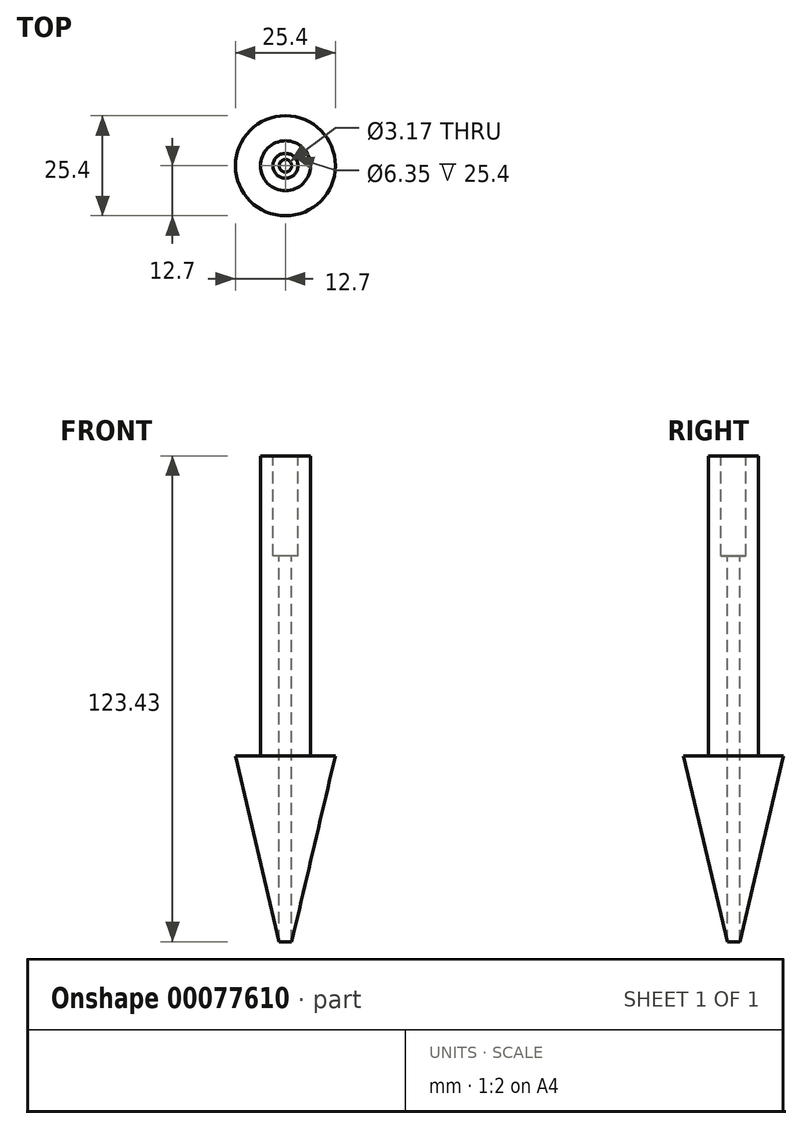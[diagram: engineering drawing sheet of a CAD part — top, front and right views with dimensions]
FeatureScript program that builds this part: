
annotation { "Feature Type Name" : "Feature", "Feature Type Description" : "" }
export const myFeature = defineFeature(function(context is Context, id is Id, definition is map)
    precondition{}
    {
        {
            var Q0;
            Q0=qCreatedBy(makeId("Front.planeOp"),FACE);
            var sketch = newSketch(context, id + "F0", { "sketchPlane" : qUnion([Q0])});
            skLineSegment(sketch, "E0", {"start": v(0, 0) * mm, "end": v(0, -53.97) * mm});
            skLineSegment(sketch, "E1", {"start": v(0, -53.98) * mm, "end": v(-12.7, 0) * mm});
            skLineSegment(sketch, "E2", {"start": v(-12.7, 0) * mm, "end": v(-6.35, 0) * mm});
            skLineSegment(sketch, "E3", {"start": v(-6.35, 0) * mm, "end": v(-6.35, 76.2) * mm});
            skLineSegment(sketch, "E4", {"start": v(-6.35, 76.2) * mm, "end": v(0, 76.2) * mm});
            skLineSegment(sketch, "E5", {"start": v(0, 76.2) * mm, "end": v(0, 0) * mm});
            skSolve(sketch);
        }
        {
            var Q0;
            Q0 = qSketchRegion(id + "F0", true);
            var Q1;
            Q1=sQuery(id+"F0.wireOp",EDGE,"E5");
            revolve(context, id + "F1", {"entities" : qUnion([Q0]), "axis" : qUnion([Q1]), "revolveType" : RevolveType.FULL});
        }
        {
            var Q0;
            Q0=makeQuery(id+"F1.opRevolve","SWEPT_FACE",FACE,{"disambiguationData":[OSD([sQuery(id+"F0.wireOp",EDGE,"E4")])]});
            var sketch = newSketch(context, id + "F2", { "sketchPlane" : qUnion([Q0])});
            skCircle(sketch, "E6", {"center": v(0, 0) * mm, "radius": 1.59 * mm});
            skSolve(sketch);
        }
        {
            var Q0;
            Q0 = qSketchRegion(id + "F2", true);
            extrude(context, id + "F3", {"entities" : qUnion([Q0]), "operationType" : NewBodyOperationType.REMOVE, "endBound" : BoundingType.THROUGH_ALL, "oppositeDirection" : true, "depth" : 25.4 * mm});
        }
        {
            var Q0;
            Q0=makeQuery(id+"F1.opRevolve","SWEPT_FACE",FACE,{"disambiguationData":[OSD([sQuery(id+"F0.wireOp",EDGE,"E4")])]});
            var sketch = newSketch(context, id + "F4", { "sketchPlane" : qUnion([Q0])});
            skCircle(sketch, "E7", {"center": v(0, 0) * mm, "radius": 3.18 * mm});
            skSolve(sketch);
        }
        {
            var Q0;
            Q0 = qSketchRegion(id + "F4", true);
            extrude(context, id + "F5", {"entities" : qUnion([Q0]), "operationType" : NewBodyOperationType.REMOVE, "oppositeDirection" : true, "depth" : 25.4 * mm});
        }
    });
